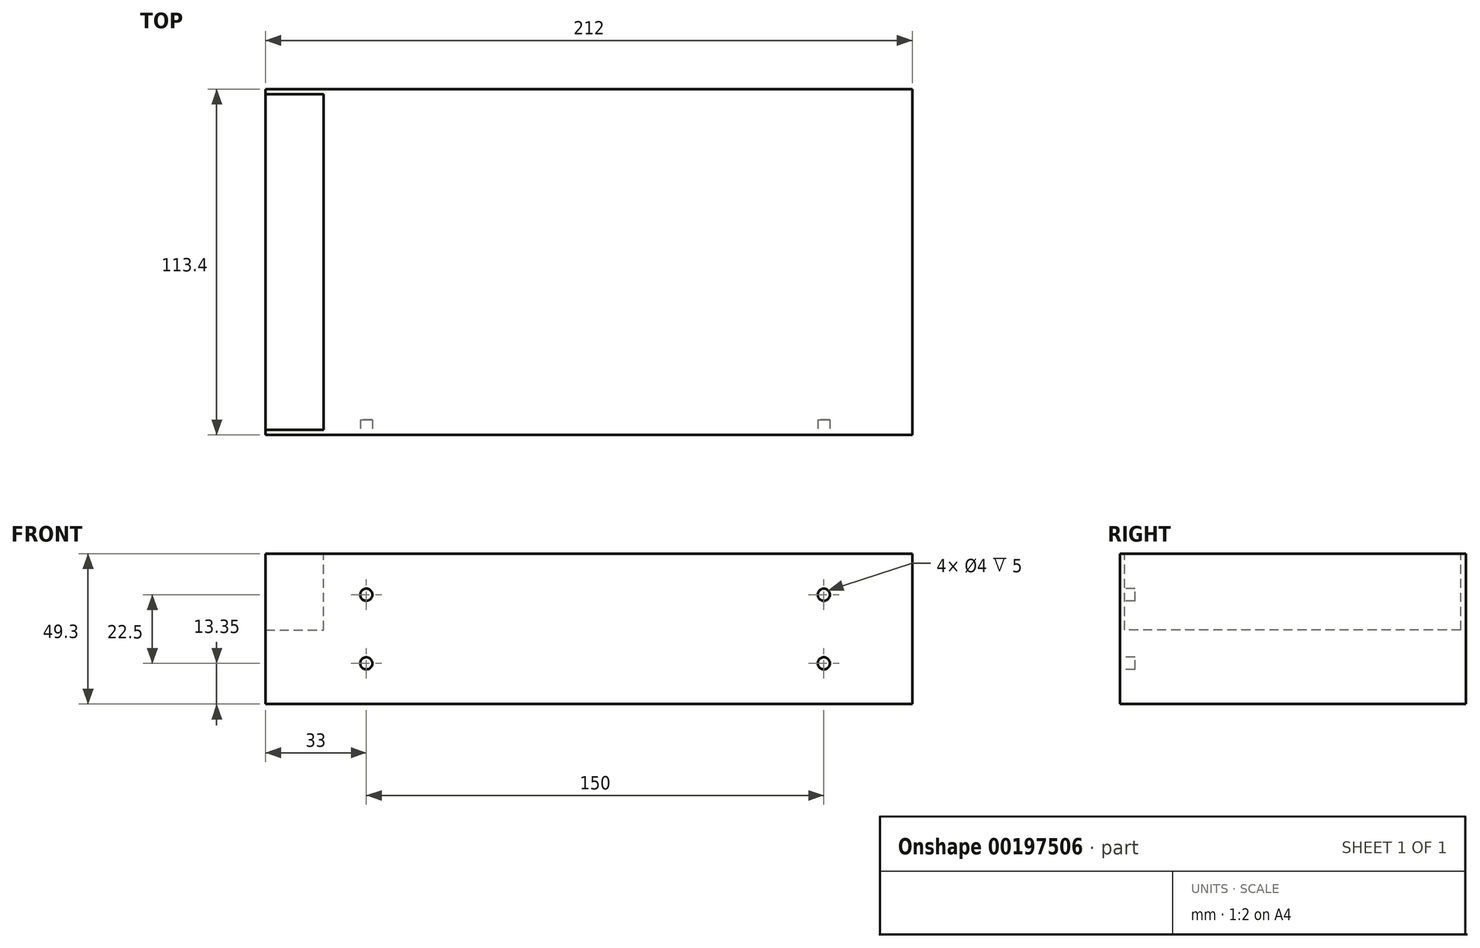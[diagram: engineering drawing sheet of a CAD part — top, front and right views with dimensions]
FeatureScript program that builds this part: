
annotation { "Feature Type Name" : "Feature", "Feature Type Description" : "" }
export const myFeature = defineFeature(function(context is Context, id is Id, definition is map)
    precondition{}
    {
        {
            var Q0;
            Q0=qCreatedBy(makeId("Top.planeOp"),FACE);
            var sketch = newSketch(context, id + "F0", { "sketchPlane" : qUnion([Q0])});
            skLineSegment(sketch, "E0.bottom", {"start": v(-106, 56.7) * mm, "end": v(106, 56.7) * mm});
            skLineSegment(sketch, "E0.top", {"start": v(-106, -56.7) * mm, "end": v(106, -56.7) * mm});
            skLineSegment(sketch, "E0.left", {"start": v(-106, 56.7) * mm, "end": v(-106, -56.7) * mm});
            skLineSegment(sketch, "E0.right", {"start": v(106, 56.7) * mm, "end": v(106, -56.7) * mm});
            skSolve(sketch);
        }
        {
            var Q0;
            Q0=qSketchRegion(id+"F0",true);
            extrude(context, id + "F1", {"entities" : qUnion([Q0]), "depth" : 49.3 * mm});
        }
        {
            var Q0;
            Q0=makeQuery(id+"F1.opExtrude","CAP_FACE",FACE,{"disambiguationData":[OSD([sQuery(id+"F0.wireOp",EDGE,"E0.bottom"),sQuery(id+"F0.wireOp",EDGE,"E0.top"),sQuery(id+"F0.wireOp",EDGE,"E0.left"),sQuery(id+"F0.wireOp",EDGE,"E0.right")])],"isStart":false});
            var sketch = newSketch(context, id + "F2", { "sketchPlane" : qUnion([Q0])});
            skLineSegment(sketch, "E1.bottom", {"start": v(-106, 55.1) * mm, "end": v(-87, 55.1) * mm});
            skLineSegment(sketch, "E1.top", {"start": v(-106, -55.1) * mm, "end": v(-87, -55.1) * mm});
            skLineSegment(sketch, "E1.left", {"start": v(-106, 55.1) * mm, "end": v(-106, -55.1) * mm});
            skLineSegment(sketch, "E1.right", {"start": v(-87, 55.1) * mm, "end": v(-87, -55.1) * mm});
            skSolve(sketch);
        }
        {
            var Q0;
            Q0=qSketchRegion(id+"F2",true);
            extrude(context, id + "F3", {"entities" : qUnion([Q0]), "operationType" : NewBodyOperationType.REMOVE, "oppositeDirection" : true, "depth" : 25 * mm});
        }
        {
            var Q0;
            Q0=makeQuery(id+"F1.opExtrude","SWEPT_FACE",FACE,{"disambiguationData":[OSD([sQuery(id+"F0.wireOp",EDGE,"E0.top")])]});
            var sketch = newSketch(context, id + "F4", { "sketchPlane" : qUnion([Q0])});
            skCircle(sketch, "E2", {"center": v(-73, 35.85) * mm, "radius": 2 * mm});
            skCircle(sketch, "E3", {"center": v(-73, 13.35) * mm, "radius": 2 * mm});
            skCircle(sketch, "E4", {"center": v(77, 35.85) * mm, "radius": 2 * mm});
            skCircle(sketch, "E5", {"center": v(77, 13.35) * mm, "radius": 2 * mm});
            skSolve(sketch);
        }
        {
            var Q0;
            Q0=qSketchRegion(id+"F4",true);
            extrude(context, id + "F5", {"entities" : qUnion([Q0]), "operationType" : NewBodyOperationType.REMOVE, "oppositeDirection" : true, "depth" : 5 * mm});
        }
    });
